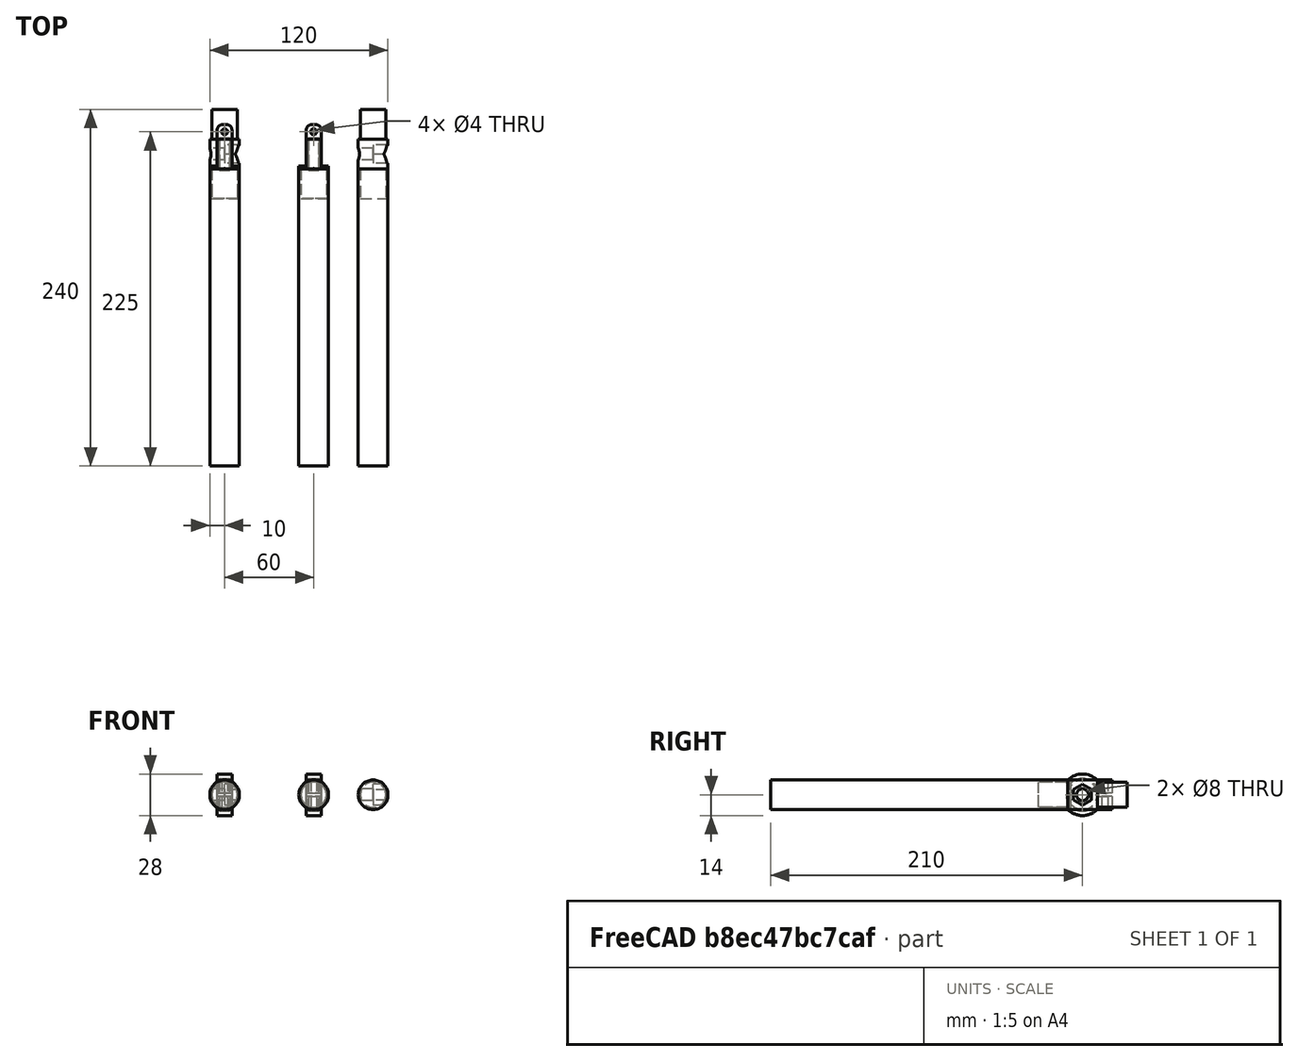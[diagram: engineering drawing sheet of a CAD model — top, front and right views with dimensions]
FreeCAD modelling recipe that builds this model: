
FCSTD DOCUMENT  (FreeCAD 0.18R16110 (Git))
Label: knee
License: All rights reserved
LicenseURL: http://en.wikipedia.org/wiki/All_rights_reserved
objects: Part::FeaturePython×4, Part::Cylinder×4, App::Part×1
note: 8 computed .brp shape members not serialized (recipe doc carries the construction recipe); baked Part::Feature solids carry a one-line shape summary decoded from their .brp

FEATURE [Part::FeaturePython] b_connector_m8_001_  label="connector-m8_001"  # a2plus imported part (geometry in sourceFile) (typed FeaturePython)
  a2p_Version = V0.1
  fixedPosition = true
  sourceFile = ./../connectors/connector-m8.FCStd
  subassemblyImport = false
  timeLastImport = 1.55919e+09
  updateColors = true
FEATURE [Part::FeaturePython] b_connector_bearing_001_  label="connector-bearing_001"  # a2plus imported part (geometry in sourceFile) (typed FeaturePython)
  Placement = pos=(0,0,0) rot=(0,1,0;1.5708rad)
  a2p_Version = V0.1
  fixedPosition = false
  sourceFile = ./../connectors/connector-bearing.FCStd
  subassemblyImport = false
  timeLastImport = 1.55919e+09
  updateColors = true
FEATURE [Part::Cylinder] Cylinder
  Angle = 360
  AttacherType = Attacher::AttachEngine3D
  Height = 200
  Placement = pos=(0,-10,2.2e-15) rot=(1,0,0;1.5708rad)
  Radius = 10
FEATURE [Part::Cylinder] Cylinder001
  Angle = 360
  AttacherType = Attacher::AttachEngine3D
  Height = 200
  Placement = pos=(0,-10,2.2e-15) rot=(1,0,0;1.5708rad)
  Radius = 10
FEATURE [Part::Cylinder] Cylinder002
  Angle = 360
  AttacherType = Attacher::AttachEngine3D
  Height = 200
  Placement = pos=(100,-10,2.2e-15) rot=(1,0,0;1.5708rad)
  Radius = 10
FEATURE [Part::FeaturePython] b_connector_m8_001_001  label="connector-m8_002"  # a2plus imported part (geometry in sourceFile) (typed FeaturePython)
  Placement = pos=(100,0,0) rot=(0,0,1;0rad)
  a2p_Version = V0.1
  fixedPosition = true
  sourceFile = ./../connectors/connector-m8.FCStd
  subassemblyImport = false
  timeLastImport = 1.55919e+09
  updateColors = true
FEATURE [Part::FeaturePython] b_connector_bearing_001_001  label="connector-bearing_002"  # a2plus imported part (geometry in sourceFile) (typed FeaturePython)
  Placement = pos=(60,0,1.33e-14) rot=(0,1,0;1.5708rad)
  a2p_Version = V0.1
  fixedPosition = false
  sourceFile = ./../connectors/connector-bearing.FCStd
  subassemblyImport = false
  timeLastImport = 1.55919e+09
  updateColors = true
FEATURE [Part::Cylinder] Cylinder003
  Angle = 360
  AttacherType = Attacher::AttachEngine3D
  Height = 200
  Placement = pos=(60,-10,2.2e-15) rot=(1,0,0;1.5708rad)
  Radius = 10
FEATURE [App::Part] Part
  Group = -> [b_connector_bearing_001_,Cylinder001,b_connector_bearing_001_001,Cylinder003]
  Origin = -> Origin
  Placement = pos=(20,0,0) rot=(1,0,0;4.71239rad)
